# Revit family: HERZ-Thermostatkopf MINI-D M28x1.5 9200 99
name_source: partatom
category: Rohrzubehör
revit_build: Autodesk Revit 2018 (Build: 20190510_1515(x64)
units: mm (PartAtom-declared; Revit-internal decimal feet)

## family parameters
Arbeitsebenenbasiert = Nein
Beim Laden mit Abzugskörper schneiden = Nein
Bemaßung runder Anschluss = Durchmesser verwenden
Gemeinsam genutzt = Nein
Immer vertikal = Nein
OmniClass-Nummer = 23.65.55.14
OmniClass-Titel = Valves for Liquid Services
Teiletyp = Normal

## types (1)
- HERZ-Thermostatkopf MINI-D M28x1.5 9200 99
    Anwendungen = Zur Montage auf Ventilen, die für thermostatischen Betrieb geeignet sind.
    Ausführungen = HERZ-Design-Thermostatkopf MINI „D“, mit Flüssigkeitsfühler (Hydrosensor).
Nur in Kombination mit Ventilheizkörper (z.B. Vogel & Noot) geeignet.
Farbe: weiß
    Bestellnummer = 1920099
    Funktionsweise = Der HERZ-Thermostat dient als Fühl- und Regelelement. Durch die Volumsänderung der Flüssigkeitsfüllung
im HERZ-Hydrosensor wird die Schubspindel des Ventils bewegt.
    Hersteller = HERZ Armaturen Ges.m.b.H.
    LO1 = 5.5 mm  [stored 0.0180446 ft]
    LO2 = 18.6 mm  [stored 0.0610236 ft]
    S01 = 91.7 mm  [stored 0.300853 ft]
    S02 = 60 mm  [stored 0.19685 ft]
    Temperatur Sollwertbereich = 6-28°C
    Thermostatkopf = Kunststoff, weiß
    URL = www.herz-armaturen.at
    automatische Frostsicherung = bei ca. 6°C

note: [stored X ft] marks values corroborated as IEEE doubles in the binary element streams (Revit-internal decimal feet)
